# Revit family: 51503232H21
name_source: partatom
category: Plumbing Fixtures
revit_build: Autodesk Revit Architecture 2012 (Build: 20110309_2315(x64)
units: mm (PartAtom-declared; Revit-internal decimal feet)

## types (1)
- 515/053232H21
    Aerator = C-M22X1
    Angle regulating valves = 232-10
    Assembly Code = D2010
    Blue headpart only = S-21-1CLOCK
    Blue headpart complete = S-21-CLOCK
    CW Connection = Yes
    CWFU = 0
    Cost = 0 $
    Default Elevation = 0' - 0"
    Description = Elbow action + A/valves + hook. Fixed centres. Swivel outlet. 1/2"BSP male inlet
    HW Connection = Yes
    HWFU = 0
    Keynote = Ideal for medical, kitchen and industrial installations
    Manufacturer = COBRA
    Material = Chrome - Polished
    Model = 515/053232H21
    Range = Medical Elbow Action
    Red headpart only = S-21-2ANTI
    Red headpart complete = S-21-ANTI
    Swan neck swivel outlet = S-044
    Type Comments = SANS 226 TYPE 2
    URL = http://www.cobra.co.za
    Vent Connection = No
    WFU = 0
    Waste Connection = No

## geometry (parser evidence)
native form markers: Blend x3
no freeform markers — native parametric forms only
